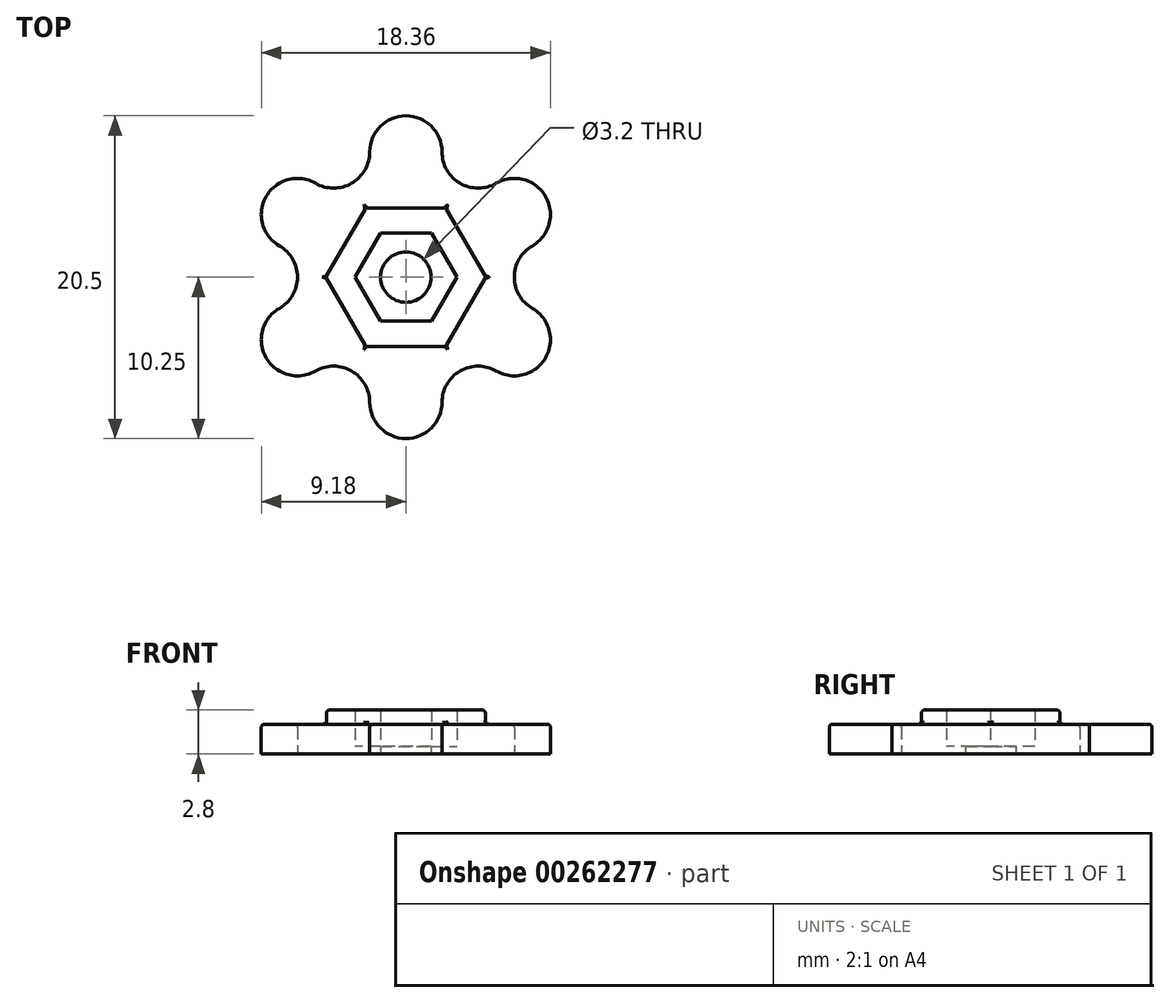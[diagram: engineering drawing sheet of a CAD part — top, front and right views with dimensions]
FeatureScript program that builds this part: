
annotation { "Feature Type Name" : "Feature", "Feature Type Description" : "" }
export const myFeature = defineFeature(function(context is Context, id is Id, definition is map)
    precondition{}
    {
        {
            var Q0;
            Q0=qCreatedBy(makeId("Top.planeOp"),FACE);
            var sketch = newSketch(context, id + "F0", { "sketchPlane" : qUnion([Q0])});
            skCircle(sketch, "E0", {"center": v(0, 0) * mm, "radius": 8.28 * mm, "construction": true});
            skArc(sketch, "E1", {"start": v(2.3, 7.95) * mm, "mid": v(0, 10.25) * mm, "end": v(-2.3, 7.95) * mm});
            skLineSegment(sketch, "E2", {"start": v(2.3, 7.95) * mm, "end": v(-2.3, 7.95) * mm, "construction": true});
            skArc(sketch, "E3", {"start": v(2.3, 7.95) * mm, "mid": v(3.44, 5.97) * mm, "end": v(5.74, 5.97) * mm});
            skLineSegment(sketch, "E4", {"start": v(2.3, 7.95) * mm, "end": v(5.74, 5.97) * mm, "construction": true});
            skArc(sketch, "E5.1.0", {"start": v(-5.74, 5.97) * mm, "mid": v(-8.88, 5.13) * mm, "end": v(-8.04, 1.99) * mm});
            skArc(sketch, "E5.1.1", {"start": v(-5.74, 5.97) * mm, "mid": v(-3.44, 5.97) * mm, "end": v(-2.3, 7.95) * mm});
            skArc(sketch, "E5.2.0", {"start": v(-8.04, -1.99) * mm, "mid": v(-8.88, -5.13) * mm, "end": v(-5.74, -5.97) * mm});
            skArc(sketch, "E5.2.1", {"start": v(-8.04, -1.99) * mm, "mid": v(-6.89, 0) * mm, "end": v(-8.04, 1.99) * mm});
            skArc(sketch, "E5.3.0", {"start": v(-2.3, -7.95) * mm, "mid": v(0, -10.25) * mm, "end": v(2.3, -7.95) * mm});
            skArc(sketch, "E5.3.1", {"start": v(-2.3, -7.95) * mm, "mid": v(-3.44, -5.97) * mm, "end": v(-5.74, -5.97) * mm});
            skArc(sketch, "E5.4.0", {"start": v(5.74, -5.97) * mm, "mid": v(8.88, -5.13) * mm, "end": v(8.04, -1.99) * mm});
            skArc(sketch, "E5.4.1", {"start": v(5.74, -5.97) * mm, "mid": v(3.44, -5.97) * mm, "end": v(2.3, -7.95) * mm});
            skArc(sketch, "E5.5.0", {"start": v(8.04, 1.99) * mm, "mid": v(8.88, 5.13) * mm, "end": v(5.74, 5.97) * mm});
            skArc(sketch, "E5.5.1", {"start": v(8.04, 1.99) * mm, "mid": v(6.89, 0) * mm, "end": v(8.04, -1.99) * mm});
            skCircle(sketch, "E6.cCircle", {"center": v(0, 0) * mm, "radius": 4.4 * mm, "construction": true});
            skLineSegment(sketch, "E6.0", {"start": v(2.54, 4.4) * mm, "end": v(5.08, 0) * mm});
            skLineSegment(sketch, "E6.1", {"start": v(5.08, 0) * mm, "end": v(2.54, -4.4) * mm});
            skLineSegment(sketch, "E6.2", {"start": v(2.54, -4.4) * mm, "end": v(-2.54, -4.4) * mm});
            skLineSegment(sketch, "E6.3", {"start": v(-2.54, -4.4) * mm, "end": v(-5.08, 0) * mm});
            skLineSegment(sketch, "E6.4", {"start": v(-5.08, 0) * mm, "end": v(-2.54, 4.4) * mm});
            skLineSegment(sketch, "E6.5", {"start": v(-2.54, 4.4) * mm, "end": v(2.54, 4.4) * mm});
            skPoint(sketch, "E6.0.midPoint", {"position": v(3.81, 2.2) * mm});
            skCircle(sketch, "E7.cCircle", {"center": v(0, 0) * mm, "radius": 2.8 * mm, "construction": true});
            skLineSegment(sketch, "E7.0", {"start": v(1.62, 2.8) * mm, "end": v(3.23, 0) * mm});
            skLineSegment(sketch, "E7.1", {"start": v(3.23, 0) * mm, "end": v(1.62, -2.8) * mm});
            skLineSegment(sketch, "E7.2", {"start": v(1.62, -2.8) * mm, "end": v(-1.62, -2.8) * mm});
            skLineSegment(sketch, "E7.3", {"start": v(-1.62, -2.8) * mm, "end": v(-3.23, 0) * mm});
            skLineSegment(sketch, "E7.4", {"start": v(-3.23, 0) * mm, "end": v(-1.62, 2.8) * mm});
            skLineSegment(sketch, "E7.5", {"start": v(-1.62, 2.8) * mm, "end": v(1.62, 2.8) * mm});
            skPoint(sketch, "E7.0.midPoint", {"position": v(2.42, 1.4) * mm});
            skCircle(sketch, "E8", {"center": v(0, 0) * mm, "radius": 1.6 * mm});
            skSolve(sketch);
        }
        {
            var Q0;
            Q0=makeQuery(id+"F0.imprint","IMPRINT",FACE,{"disambiguationData":[TD([[makeQuery(id+"F0.imprint","IMPRINT",EDGE,{"derivedFrom":sQuery(id+"F0.wireOp",EDGE,"E1")}),1.0]])]});
            extrude(context, id + "F1", {"entities" : qUnion([Q0]), "depth" : 1.9 * mm});
        }
        {
            var Q0;
            Q0=makeQuery(id+"F0.imprint","IMPRINT",FACE,{"disambiguationData":[TD([[makeQuery(id+"F0.imprint","IMPRINT",EDGE,{"derivedFrom":sQuery(id+"F0.wireOp",EDGE,"E6.0")}),-1.0]])]});
            extrude(context, id + "F2", {"entities" : qUnion([Q0]), "operationType" : NewBodyOperationType.ADD, "depth" : 2.8 * mm});
        }
        {
            var Q0;
            Q0=makeQuery(id+"F0.imprint","IMPRINT",FACE,{"disambiguationData":[TD([[makeQuery(id+"F0.imprint","IMPRINT",EDGE,{"derivedFrom":sQuery(id+"F0.wireOp",EDGE,"E7.0")}),-1.0]])]});
            extrude(context, id + "F3", {"entities" : qUnion([Q0]), "operationType" : NewBodyOperationType.ADD, "depth" : 0.5 * mm});
        }
        {
            var Q0;
            Q0=makeQuery(id+"F1.opExtrude","CAP_FACE",FACE,{"disambiguationData":[OSD([sQuery(id+"F0.wireOp",EDGE,"E1"),sQuery(id+"F0.wireOp",EDGE,"E3"),sQuery(id+"F0.wireOp",EDGE,"E5.1.0"),sQuery(id+"F0.wireOp",EDGE,"E5.1.1"),sQuery(id+"F0.wireOp",EDGE,"E5.2.0"),sQuery(id+"F0.wireOp",EDGE,"E5.2.1"),sQuery(id+"F0.wireOp",EDGE,"E5.3.0"),sQuery(id+"F0.wireOp",EDGE,"E5.3.1"),sQuery(id+"F0.wireOp",EDGE,"E5.4.0"),sQuery(id+"F0.wireOp",EDGE,"E5.4.1"),sQuery(id+"F0.wireOp",EDGE,"E5.5.0"),sQuery(id+"F0.wireOp",EDGE,"E5.5.1"),sQuery(id+"F0.wireOp",EDGE,"E6.0"),sQuery(id+"F0.wireOp",EDGE,"E6.1"),sQuery(id+"F0.wireOp",EDGE,"E6.2"),sQuery(id+"F0.wireOp",EDGE,"E6.3"),sQuery(id+"F0.wireOp",EDGE,"E6.4"),sQuery(id+"F0.wireOp",EDGE,"E6.5")])],"isStart":false});
            fillet(context, id + "F4", {"entities" : qUnion([Q0]), "radius" : 0.2 * mm, "tangentPropagation" : true, "allowEdgeOverflow" : false});
        }
        {
            var Q0;
            Q0=makeQuery(id+"F2.opExtrude","CAP_EDGE",EDGE,{"disambiguationData":[OSD([sQuery(id+"F0.wireOp",EDGE,"E6.1")])],"isStart":false});
            var Q1;
            Q1=makeQuery(id+"F2.opExtrude","SWEPT_EDGE",EDGE,{"disambiguationData":[OSD([sQuery(id+"F0.wireOp",EDGE,"E6.1"),sQuery(id+"F0.wireOp",EDGE,"E6.2")])]});
            var Q2;
            Q2=makeQuery(id+"F2.opExtrude","CAP_EDGE",EDGE,{"disambiguationData":[OSD([sQuery(id+"F0.wireOp",EDGE,"E6.2")])],"isStart":false});
            var Q3;
            Q3=makeQuery(id+"F2.opExtrude","SWEPT_EDGE",EDGE,{"disambiguationData":[OSD([sQuery(id+"F0.wireOp",EDGE,"E6.2"),sQuery(id+"F0.wireOp",EDGE,"E6.3")])]});
            var Q4;
            Q4=makeQuery(id+"F2.opExtrude","CAP_EDGE",EDGE,{"disambiguationData":[OSD([sQuery(id+"F0.wireOp",EDGE,"E6.3")])],"isStart":false});
            var Q5;
            Q5=makeQuery(id+"F2.opExtrude","CAP_EDGE",EDGE,{"disambiguationData":[OSD([sQuery(id+"F0.wireOp",EDGE,"E6.4")])],"isStart":false});
            var Q6;
            Q6=makeQuery(id+"F2.opExtrude","SWEPT_EDGE",EDGE,{"disambiguationData":[OSD([sQuery(id+"F0.wireOp",EDGE,"E6.3"),sQuery(id+"F0.wireOp",EDGE,"E6.4")])]});
            var Q7;
            Q7=makeQuery(id+"F2.opExtrude","SWEPT_EDGE",EDGE,{"disambiguationData":[OSD([sQuery(id+"F0.wireOp",EDGE,"E6.4"),sQuery(id+"F0.wireOp",EDGE,"E6.5")])]});
            var Q8;
            Q8=makeQuery(id+"F2.opExtrude","CAP_EDGE",EDGE,{"disambiguationData":[OSD([sQuery(id+"F0.wireOp",EDGE,"E6.5")])],"isStart":false});
            var Q9;
            Q9=makeQuery(id+"F2.opExtrude","SWEPT_EDGE",EDGE,{"disambiguationData":[OSD([sQuery(id+"F0.wireOp",EDGE,"E6.0"),sQuery(id+"F0.wireOp",EDGE,"E6.5")])]});
            var Q10;
            Q10=makeQuery(id+"F2.opExtrude","CAP_EDGE",EDGE,{"disambiguationData":[OSD([sQuery(id+"F0.wireOp",EDGE,"E6.0")])],"isStart":false});
            var Q11;
            Q11=makeQuery(id+"F2.opExtrude","SWEPT_EDGE",EDGE,{"disambiguationData":[OSD([sQuery(id+"F0.wireOp",EDGE,"E6.0"),sQuery(id+"F0.wireOp",EDGE,"E6.1")])]});
            fillet(context, id + "F5", {"entities" : qUnion([Q0, Q1, Q2, Q3, Q4, Q5, Q6, Q7, Q8, Q9, Q10, Q11]), "radius" : 0.2 * mm, "tangentPropagation" : true, "allowEdgeOverflow" : false});
        }
    });
